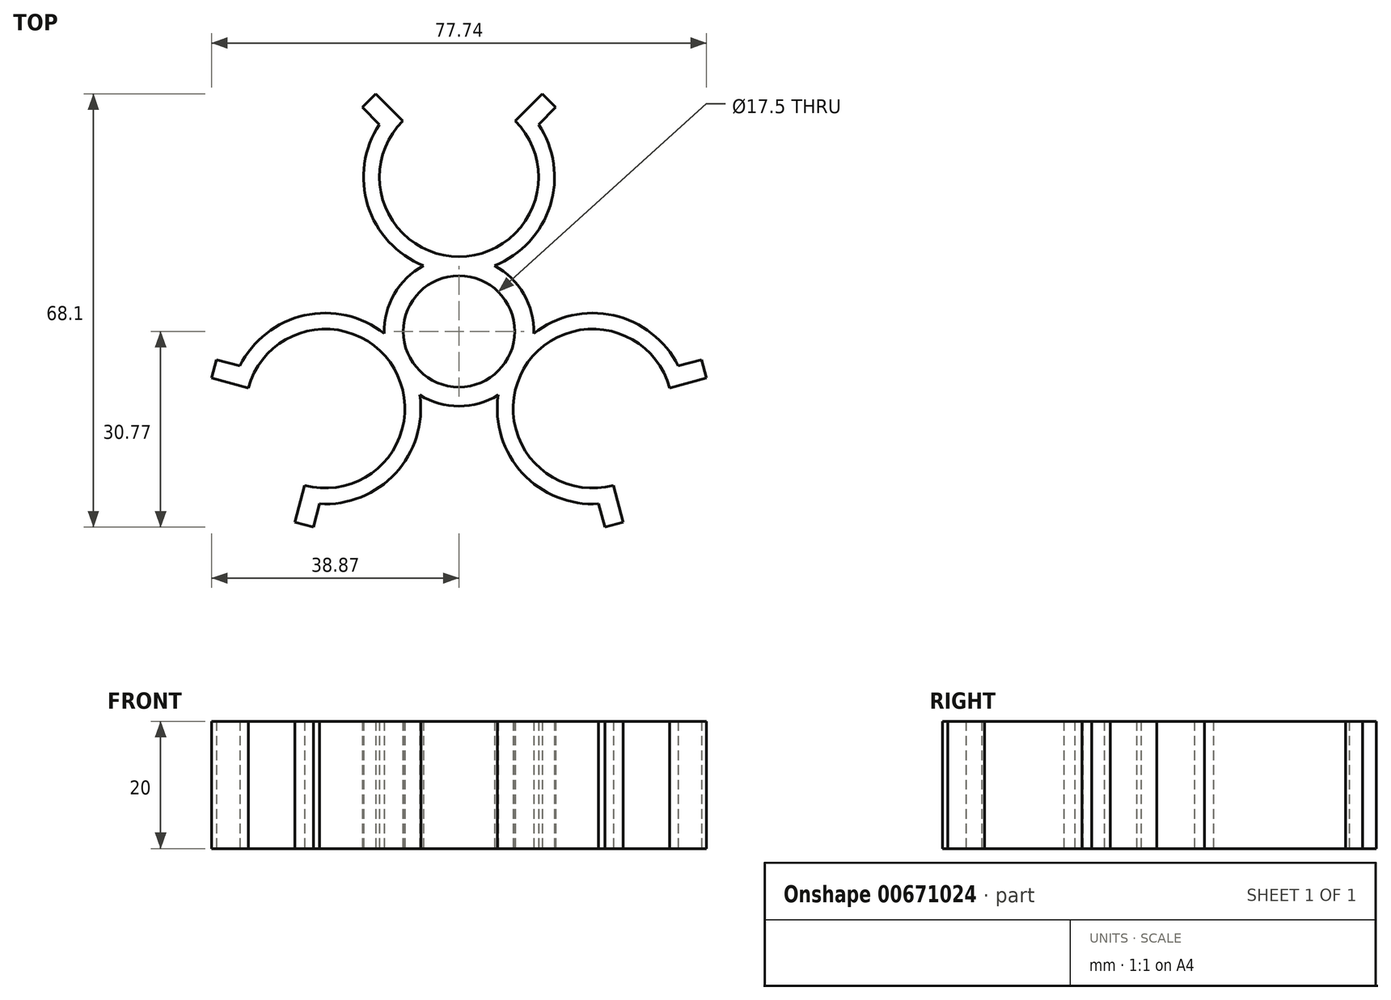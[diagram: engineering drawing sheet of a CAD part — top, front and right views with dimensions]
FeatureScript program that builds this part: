
annotation { "Feature Type Name" : "Feature", "Feature Type Description" : "" }
export const myFeature = defineFeature(function(context is Context, id is Id, definition is map)
    precondition{}
    {
        {
            var Q0;
            Q0=qCreatedBy(makeId("Top.planeOp"),FACE);
            var sketch = newSketch(context, id + "F0", { "sketchPlane" : qUnion([Q0])});
            skArc(sketch, "E0", {"start": v(-8.84, 33.09) * mm, "mid": v(0, 11.75) * mm, "end": v(8.84, 33.09) * mm});
            skArc(sketch, "E1", {"start": v(12.51, 32.52) * mm, "mid": v(14.32, 19.78) * mm, "end": v(5.6, 10.33) * mm});
            skLineSegment(sketch, "E2", {"start": v(-8.84, 33.09) * mm, "end": v(-13.08, 37.33) * mm});
            skLineSegment(sketch, "E3", {"start": v(-13.08, 37.33) * mm, "end": v(-15.2, 35.2) * mm});
            skLineSegment(sketch, "E4", {"start": v(-15.2, 35.2) * mm, "end": v(-12.51, 32.52) * mm});
            skLineSegment(sketch, "E5.MirrorCS", {"start": v(8.84, 33.09) * mm, "end": v(13.08, 37.33) * mm});
            skLineSegment(sketch, "E6.MirrorCS", {"start": v(15.2, 35.2) * mm, "end": v(12.51, 32.52) * mm});
            skLineSegment(sketch, "E7.MirrorCS", {"start": v(13.08, 37.33) * mm, "end": v(15.2, 35.2) * mm});
            skLineSegment(sketch, "E8.1.0", {"start": v(-33.07, -8.89) * mm, "end": v(-38.87, -7.34) * mm});
            skArc(sketch, "E8.1.1", {"start": v(-24.24, -24.2) * mm, "mid": v(-10.17, -5.87) * mm, "end": v(-33.07, -8.89) * mm});
            skArc(sketch, "E8.1.2", {"start": v(-34.42, -5.42) * mm, "mid": v(-24.3, 2.5) * mm, "end": v(-11.74, -0.32) * mm});
            skLineSegment(sketch, "E8.1.3", {"start": v(-24.24, -24.2) * mm, "end": v(-25.79, -30) * mm});
            skLineSegment(sketch, "E8.1.4", {"start": v(-38.1, -4.44) * mm, "end": v(-34.42, -5.42) * mm});
            skLineSegment(sketch, "E8.1.5", {"start": v(-25.79, -30) * mm, "end": v(-22.9, -30.77) * mm});
            skLineSegment(sketch, "E8.1.6", {"start": v(-22.9, -30.77) * mm, "end": v(-21.9, -27.1) * mm});
            skLineSegment(sketch, "E8.1.7", {"start": v(-38.87, -7.34) * mm, "end": v(-38.1, -4.44) * mm});
            skLineSegment(sketch, "E8.2.0", {"start": v(24.24, -24.2) * mm, "end": v(25.79, -30) * mm});
            skArc(sketch, "E8.2.1", {"start": v(33.07, -8.89) * mm, "mid": v(10.17, -5.87) * mm, "end": v(24.24, -24.2) * mm});
            skArc(sketch, "E8.2.2", {"start": v(21.9, -27.1) * mm, "mid": v(9.97, -22.3) * mm, "end": v(6.15, -10.01) * mm});
            skLineSegment(sketch, "E8.2.3", {"start": v(33.07, -8.89) * mm, "end": v(38.87, -7.34) * mm});
            skLineSegment(sketch, "E8.2.4", {"start": v(22.9, -30.77) * mm, "end": v(21.9, -27.1) * mm});
            skLineSegment(sketch, "E8.2.5", {"start": v(38.87, -7.34) * mm, "end": v(38.1, -4.44) * mm});
            skLineSegment(sketch, "E8.2.6", {"start": v(38.1, -4.44) * mm, "end": v(34.42, -5.42) * mm});
            skLineSegment(sketch, "E8.2.7", {"start": v(25.79, -30) * mm, "end": v(22.9, -30.77) * mm});
            skPoint(sketch, "E8.center", {"position": v(0, 0) * mm});
            skCircle(sketch, "E9", {"center": v(0, 0) * mm, "radius": 8.75 * mm});
            skArc(sketch, "E10", {"start": v(-6.15, -10.01) * mm, "mid": v(0, -11.75) * mm, "end": v(6.15, -10.01) * mm});
            skArc(sketch, "E11.trimOffspring", {"start": v(-6.15, -10.01) * mm, "mid": v(-9.97, -22.3) * mm, "end": v(-21.9, -27.1) * mm});
            skArc(sketch, "E12.trimOffspring", {"start": v(-5.6, 10.33) * mm, "mid": v(-10.17, 5.87) * mm, "end": v(-11.74, -0.32) * mm});
            skArc(sketch, "E13.trimOffspring", {"start": v(-5.6, 10.33) * mm, "mid": v(-14.32, 19.78) * mm, "end": v(-12.51, 32.52) * mm});
            skArc(sketch, "E14.trimOffspring", {"start": v(11.74, -0.32) * mm, "mid": v(24.3, 2.5) * mm, "end": v(34.42, -5.42) * mm});
            skArc(sketch, "E15.trimOffspring", {"start": v(11.74, -0.32) * mm, "mid": v(10.17, 5.87) * mm, "end": v(5.6, 10.33) * mm});
            skSolve(sketch);
        }
        {
            var Q0;
            Q0 = qSketchRegion(id + "F0", true);
            extrude(context, id + "F1", {"entities" : qUnion([Q0]), "depth" : 20 * mm, "offsetDistance" : 25 * mm});
        }
    });
